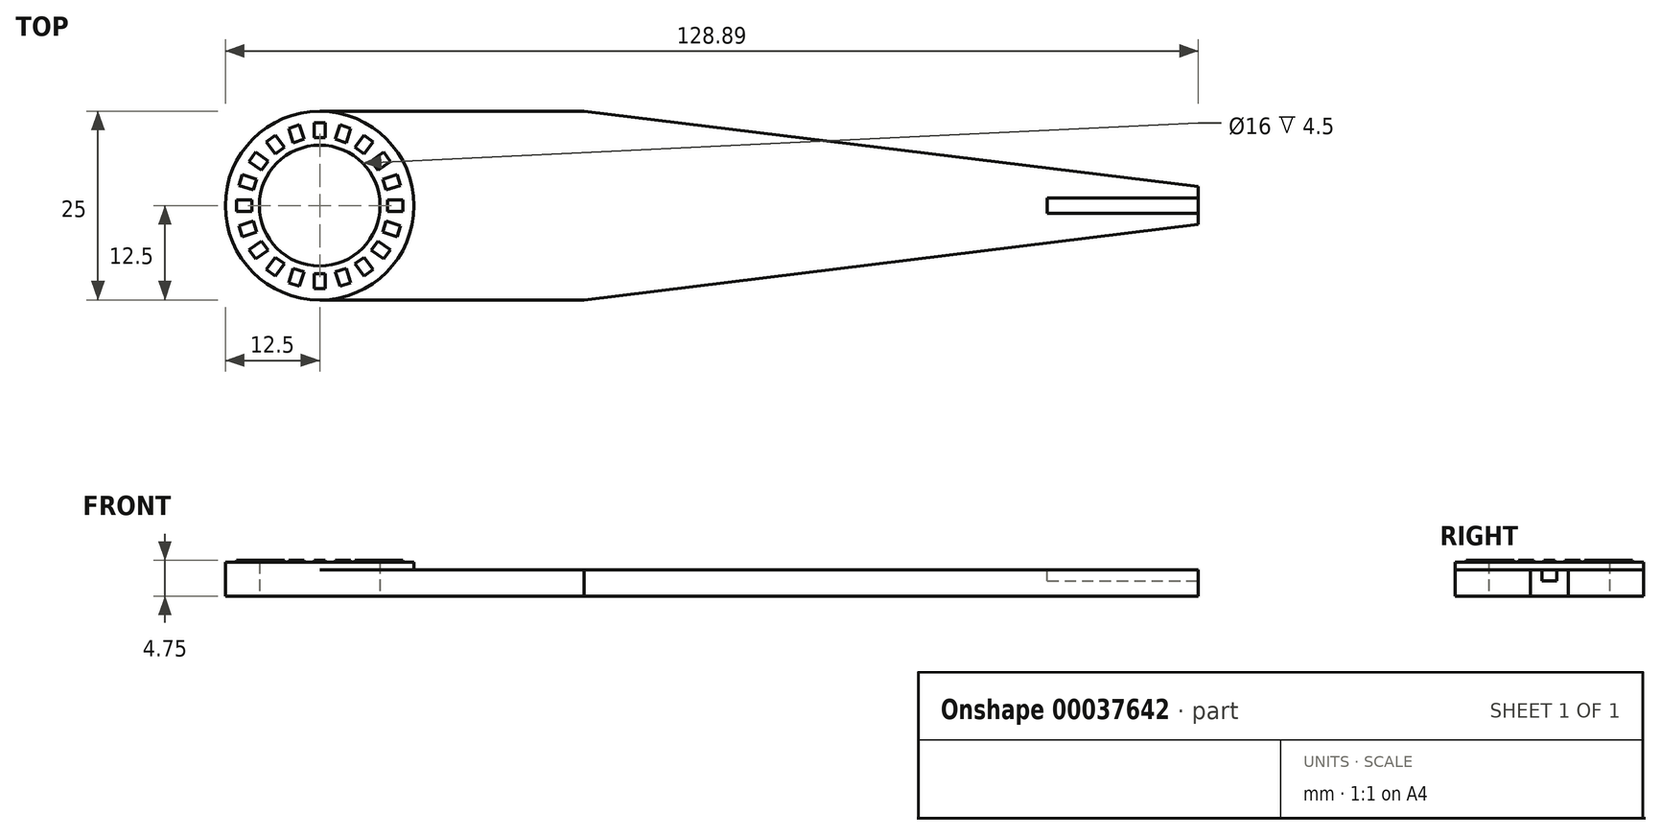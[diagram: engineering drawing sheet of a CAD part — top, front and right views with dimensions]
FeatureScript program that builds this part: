
annotation { "Feature Type Name" : "Feature", "Feature Type Description" : "" }
export const myFeature = defineFeature(function(context is Context, id is Id, definition is map)
    precondition{}
    {
        {
            var Q0;
            Q0=qCreatedBy(makeId("Top.planeOp"),FACE);
            var sketch = newSketch(context, id + "F0", { "sketchPlane" : qUnion([Q0])});
            skCircle(sketch, "E0", {"center": v(0, 0) * mm, "radius": 12.5 * mm});
            skCircle(sketch, "E1", {"center": v(0, 0) * mm, "radius": 8 * mm});
            skLineSegment(sketch, "E2", {"start": v(0, 12.5) * mm, "end": v(35, 12.5) * mm});
            skLineSegment(sketch, "E3", {"start": v(0, 0) * mm, "end": v(42.2, 0) * mm, "construction": true});
            skLineSegment(sketch, "E4.MirrorCS", {"start": v(0, -12.5) * mm, "end": v(35, -12.5) * mm});
            skLineSegment(sketch, "E5", {"start": v(35, 12.5) * mm, "end": v(116.39, 2.5) * mm});
            skLineSegment(sketch, "E6", {"start": v(35, 12.5) * mm, "end": v(94.74, 12.5) * mm, "construction": true});
            skLineSegment(sketch, "E7.MirrorCS", {"start": v(35, -12.5) * mm, "end": v(116.39, -2.5) * mm});
            skLineSegment(sketch, "E8", {"start": v(116.39, 2.5) * mm, "end": v(116.39, -2.5) * mm});
            skSolve(sketch);
        }
        {
            var Q0;
            Q0 = qSketchRegion(id + "F0", true);
            extrude(context, id + "F1", {"entities" : qUnion([Q0]), "depth" : 3.5 * mm});
        }
        {
            var Q0;
            Q0=makeQuery(id+"F1.opExtrude","CAP_FACE",FACE,{"disambiguationData":[OSD([sQuery(id+"F0.wireOp",EDGE,"E0"),sQuery(id+"F0.wireOp",EDGE,"E1"),sQuery(id+"F0.wireOp",EDGE,"E2"),sQuery(id+"F0.wireOp",EDGE,"E4.MirrorCS"),sQuery(id+"F0.wireOp",EDGE,"E5"),sQuery(id+"F0.wireOp",EDGE,"E7.MirrorCS"),sQuery(id+"F0.wireOp",EDGE,"E8")])],"isStart":false});
            var sketch = newSketch(context, id + "F2", { "sketchPlane" : qUnion([Q0])});
            skCircle(sketch, "E9", {"center": v(0, 0) * mm, "radius": 8 * mm});
            skCircle(sketch, "E10", {"center": v(0, 0) * mm, "radius": 12.5 * mm});
            skSolve(sketch);
        }
        {
            var Q0;
            Q0 = qSketchRegion(id + "F2", true);
            extrude(context, id + "F3", {"entities" : qUnion([Q0]), "operationType" : NewBodyOperationType.ADD, "depth" : 1 * mm});
        }
        {
            var Q0;
            Q0=makeQuery(id+"F3.opExtrude","CAP_FACE",FACE,{"disambiguationData":[OSD([sQuery(id+"F2.wireOp",EDGE,"E9"),sQuery(id+"F2.wireOp",EDGE,"E10")])],"isStart":false});
            var sketch = newSketch(context, id + "F4", { "sketchPlane" : qUnion([Q0])});
            skLineSegment(sketch, "E11.bottom", {"start": v(-0.75, 11) * mm, "end": v(0.75, 11) * mm});
            skLineSegment(sketch, "E11.top", {"start": v(-0.75, 9) * mm, "end": v(0.75, 9) * mm});
            skLineSegment(sketch, "E11.left", {"start": v(-0.75, 11) * mm, "end": v(-0.75, 9) * mm});
            skLineSegment(sketch, "E11.right", {"start": v(0.75, 11) * mm, "end": v(0.75, 9) * mm});
            skPoint(sketch, "E12", {"position": v(0, 8) * mm});
            skLineSegment(sketch, "E13.1.0", {"start": v(-4.11, 10.23) * mm, "end": v(-3.5, 8.33) * mm});
            skLineSegment(sketch, "E13.1.1", {"start": v(-3.5, 8.33) * mm, "end": v(-2.07, 8.8) * mm});
            skLineSegment(sketch, "E13.1.2", {"start": v(-2.69, 10.7) * mm, "end": v(-2.07, 8.8) * mm});
            skLineSegment(sketch, "E13.1.3", {"start": v(-4.11, 10.23) * mm, "end": v(-2.69, 10.7) * mm});
            skLineSegment(sketch, "E13.2.0", {"start": v(-7.07, 8.46) * mm, "end": v(-5.9, 6.84) * mm});
            skLineSegment(sketch, "E13.2.1", {"start": v(-5.9, 6.84) * mm, "end": v(-4.68, 7.72) * mm});
            skLineSegment(sketch, "E13.2.2", {"start": v(-5.86, 9.34) * mm, "end": v(-4.68, 7.72) * mm});
            skLineSegment(sketch, "E13.2.3", {"start": v(-7.07, 8.46) * mm, "end": v(-5.86, 9.34) * mm});
            skLineSegment(sketch, "E13.3.0", {"start": v(-9.34, 5.86) * mm, "end": v(-7.72, 4.68) * mm});
            skLineSegment(sketch, "E13.3.1", {"start": v(-7.72, 4.68) * mm, "end": v(-6.84, 5.9) * mm});
            skLineSegment(sketch, "E13.3.2", {"start": v(-8.46, 7.07) * mm, "end": v(-6.84, 5.9) * mm});
            skLineSegment(sketch, "E13.3.3", {"start": v(-9.34, 5.86) * mm, "end": v(-8.46, 7.07) * mm});
            skLineSegment(sketch, "E13.4.0", {"start": v(-10.7, 2.69) * mm, "end": v(-8.8, 2.07) * mm});
            skLineSegment(sketch, "E13.4.1", {"start": v(-8.8, 2.07) * mm, "end": v(-8.33, 3.5) * mm});
            skLineSegment(sketch, "E13.4.2", {"start": v(-10.23, 4.11) * mm, "end": v(-8.33, 3.5) * mm});
            skLineSegment(sketch, "E13.4.3", {"start": v(-10.7, 2.69) * mm, "end": v(-10.23, 4.11) * mm});
            skLineSegment(sketch, "E13.5.0", {"start": v(-11, -0.75) * mm, "end": v(-9, -0.75) * mm});
            skLineSegment(sketch, "E13.5.1", {"start": v(-9, -0.75) * mm, "end": v(-9, 0.75) * mm});
            skLineSegment(sketch, "E13.5.2", {"start": v(-11, 0.75) * mm, "end": v(-9, 0.75) * mm});
            skLineSegment(sketch, "E13.5.3", {"start": v(-11, -0.75) * mm, "end": v(-11, 0.75) * mm});
            skLineSegment(sketch, "E13.6.0", {"start": v(-10.23, -4.11) * mm, "end": v(-8.33, -3.5) * mm});
            skLineSegment(sketch, "E13.6.1", {"start": v(-8.33, -3.5) * mm, "end": v(-8.8, -2.07) * mm});
            skLineSegment(sketch, "E13.6.2", {"start": v(-10.7, -2.69) * mm, "end": v(-8.8, -2.07) * mm});
            skLineSegment(sketch, "E13.6.3", {"start": v(-10.23, -4.11) * mm, "end": v(-10.7, -2.69) * mm});
            skLineSegment(sketch, "E13.7.0", {"start": v(-8.46, -7.07) * mm, "end": v(-6.84, -5.9) * mm});
            skLineSegment(sketch, "E13.7.1", {"start": v(-6.84, -5.9) * mm, "end": v(-7.72, -4.68) * mm});
            skLineSegment(sketch, "E13.7.2", {"start": v(-9.34, -5.86) * mm, "end": v(-7.72, -4.68) * mm});
            skLineSegment(sketch, "E13.7.3", {"start": v(-8.46, -7.07) * mm, "end": v(-9.34, -5.86) * mm});
            skLineSegment(sketch, "E13.8.0", {"start": v(-5.86, -9.34) * mm, "end": v(-4.68, -7.72) * mm});
            skLineSegment(sketch, "E13.8.1", {"start": v(-4.68, -7.72) * mm, "end": v(-5.9, -6.84) * mm});
            skLineSegment(sketch, "E13.8.2", {"start": v(-7.07, -8.46) * mm, "end": v(-5.9, -6.84) * mm});
            skLineSegment(sketch, "E13.8.3", {"start": v(-5.86, -9.34) * mm, "end": v(-7.07, -8.46) * mm});
            skLineSegment(sketch, "E13.9.0", {"start": v(-2.69, -10.7) * mm, "end": v(-2.07, -8.8) * mm});
            skLineSegment(sketch, "E13.9.1", {"start": v(-2.07, -8.8) * mm, "end": v(-3.5, -8.33) * mm});
            skLineSegment(sketch, "E13.9.2", {"start": v(-4.11, -10.23) * mm, "end": v(-3.5, -8.33) * mm});
            skLineSegment(sketch, "E13.9.3", {"start": v(-2.69, -10.7) * mm, "end": v(-4.11, -10.23) * mm});
            skLineSegment(sketch, "E13.10.0", {"start": v(0.75, -11) * mm, "end": v(0.75, -9) * mm});
            skLineSegment(sketch, "E13.10.1", {"start": v(0.75, -9) * mm, "end": v(-0.75, -9) * mm});
            skLineSegment(sketch, "E13.10.2", {"start": v(-0.75, -11) * mm, "end": v(-0.75, -9) * mm});
            skLineSegment(sketch, "E13.10.3", {"start": v(0.75, -11) * mm, "end": v(-0.75, -11) * mm});
            skLineSegment(sketch, "E13.11.0", {"start": v(4.11, -10.23) * mm, "end": v(3.5, -8.33) * mm});
            skLineSegment(sketch, "E13.11.1", {"start": v(3.5, -8.33) * mm, "end": v(2.07, -8.8) * mm});
            skLineSegment(sketch, "E13.11.2", {"start": v(2.69, -10.7) * mm, "end": v(2.07, -8.8) * mm});
            skLineSegment(sketch, "E13.11.3", {"start": v(4.11, -10.23) * mm, "end": v(2.69, -10.7) * mm});
            skLineSegment(sketch, "E13.12.0", {"start": v(7.07, -8.46) * mm, "end": v(5.9, -6.84) * mm});
            skLineSegment(sketch, "E13.12.1", {"start": v(5.9, -6.84) * mm, "end": v(4.68, -7.72) * mm});
            skLineSegment(sketch, "E13.12.2", {"start": v(5.86, -9.34) * mm, "end": v(4.68, -7.72) * mm});
            skLineSegment(sketch, "E13.12.3", {"start": v(7.07, -8.46) * mm, "end": v(5.86, -9.34) * mm});
            skLineSegment(sketch, "E13.13.0", {"start": v(9.34, -5.86) * mm, "end": v(7.72, -4.68) * mm});
            skLineSegment(sketch, "E13.13.1", {"start": v(7.72, -4.68) * mm, "end": v(6.84, -5.9) * mm});
            skLineSegment(sketch, "E13.13.2", {"start": v(8.46, -7.07) * mm, "end": v(6.84, -5.9) * mm});
            skLineSegment(sketch, "E13.13.3", {"start": v(9.34, -5.86) * mm, "end": v(8.46, -7.07) * mm});
            skLineSegment(sketch, "E13.14.0", {"start": v(10.7, -2.69) * mm, "end": v(8.8, -2.07) * mm});
            skLineSegment(sketch, "E13.14.1", {"start": v(8.8, -2.07) * mm, "end": v(8.33, -3.5) * mm});
            skLineSegment(sketch, "E13.14.2", {"start": v(10.23, -4.11) * mm, "end": v(8.33, -3.5) * mm});
            skLineSegment(sketch, "E13.14.3", {"start": v(10.7, -2.69) * mm, "end": v(10.23, -4.11) * mm});
            skLineSegment(sketch, "E13.15.0", {"start": v(11, 0.75) * mm, "end": v(9, 0.75) * mm});
            skLineSegment(sketch, "E13.15.1", {"start": v(9, 0.75) * mm, "end": v(9, -0.75) * mm});
            skLineSegment(sketch, "E13.15.2", {"start": v(11, -0.75) * mm, "end": v(9, -0.75) * mm});
            skLineSegment(sketch, "E13.15.3", {"start": v(11, 0.75) * mm, "end": v(11, -0.75) * mm});
            skLineSegment(sketch, "E13.16.0", {"start": v(10.23, 4.11) * mm, "end": v(8.33, 3.5) * mm});
            skLineSegment(sketch, "E13.16.1", {"start": v(8.33, 3.5) * mm, "end": v(8.8, 2.07) * mm});
            skLineSegment(sketch, "E13.16.2", {"start": v(10.7, 2.69) * mm, "end": v(8.8, 2.07) * mm});
            skLineSegment(sketch, "E13.16.3", {"start": v(10.23, 4.11) * mm, "end": v(10.7, 2.69) * mm});
            skLineSegment(sketch, "E13.17.0", {"start": v(8.46, 7.07) * mm, "end": v(6.84, 5.9) * mm});
            skLineSegment(sketch, "E13.17.1", {"start": v(6.84, 5.9) * mm, "end": v(7.72, 4.68) * mm});
            skLineSegment(sketch, "E13.17.2", {"start": v(9.34, 5.86) * mm, "end": v(7.72, 4.68) * mm});
            skLineSegment(sketch, "E13.17.3", {"start": v(8.46, 7.07) * mm, "end": v(9.34, 5.86) * mm});
            skLineSegment(sketch, "E13.18.0", {"start": v(5.86, 9.34) * mm, "end": v(4.68, 7.72) * mm});
            skLineSegment(sketch, "E13.18.1", {"start": v(4.68, 7.72) * mm, "end": v(5.9, 6.84) * mm});
            skLineSegment(sketch, "E13.18.2", {"start": v(7.07, 8.46) * mm, "end": v(5.9, 6.84) * mm});
            skLineSegment(sketch, "E13.18.3", {"start": v(5.86, 9.34) * mm, "end": v(7.07, 8.46) * mm});
            skLineSegment(sketch, "E13.19.0", {"start": v(2.69, 10.7) * mm, "end": v(2.07, 8.8) * mm});
            skLineSegment(sketch, "E13.19.1", {"start": v(2.07, 8.8) * mm, "end": v(3.5, 8.33) * mm});
            skLineSegment(sketch, "E13.19.2", {"start": v(4.11, 10.23) * mm, "end": v(3.5, 8.33) * mm});
            skLineSegment(sketch, "E13.19.3", {"start": v(2.69, 10.7) * mm, "end": v(4.11, 10.23) * mm});
            skPoint(sketch, "E13.center", {"position": v(0, 0) * mm});
            skSolve(sketch);
        }
        {
            var Q0;
            Q0 = qSketchRegion(id + "F4", true);
            extrude(context, id + "F5", {"entities" : qUnion([Q0]), "operationType" : NewBodyOperationType.ADD, "depth" : .25 * mm});
        }
        {
            var Q0;
            Q0=makeQuery(id+"F1.opExtrude","CAP_FACE",FACE,{"disambiguationData":[OSD([sQuery(id+"F0.wireOp",EDGE,"E0"),sQuery(id+"F0.wireOp",EDGE,"E1"),sQuery(id+"F0.wireOp",EDGE,"E2"),sQuery(id+"F0.wireOp",EDGE,"E4.MirrorCS"),sQuery(id+"F0.wireOp",EDGE,"E5"),sQuery(id+"F0.wireOp",EDGE,"E7.MirrorCS"),sQuery(id+"F0.wireOp",EDGE,"E8")])],"isStart":false});
            var sketch = newSketch(context, id + "F6", { "sketchPlane" : qUnion([Q0])});
            skLineSegment(sketch, "E14.bottom", {"start": v(96.39, 1) * mm, "end": v(116.39, 1) * mm});
            skLineSegment(sketch, "E14.top", {"start": v(96.39, -1) * mm, "end": v(116.39, -1) * mm});
            skLineSegment(sketch, "E14.left", {"start": v(96.39, 1) * mm, "end": v(96.39, -1) * mm});
            skLineSegment(sketch, "E14.right", {"start": v(116.39, 1) * mm, "end": v(116.39, -1) * mm});
            skSolve(sketch);
        }
        {
            var Q0;
            Q0 = qSketchRegion(id + "F6", true);
            extrude(context, id + "F7", {"entities" : qUnion([Q0]), "operationType" : NewBodyOperationType.REMOVE, "oppositeDirection" : true, "depth" : 1.5 * mm});
        }
    });
